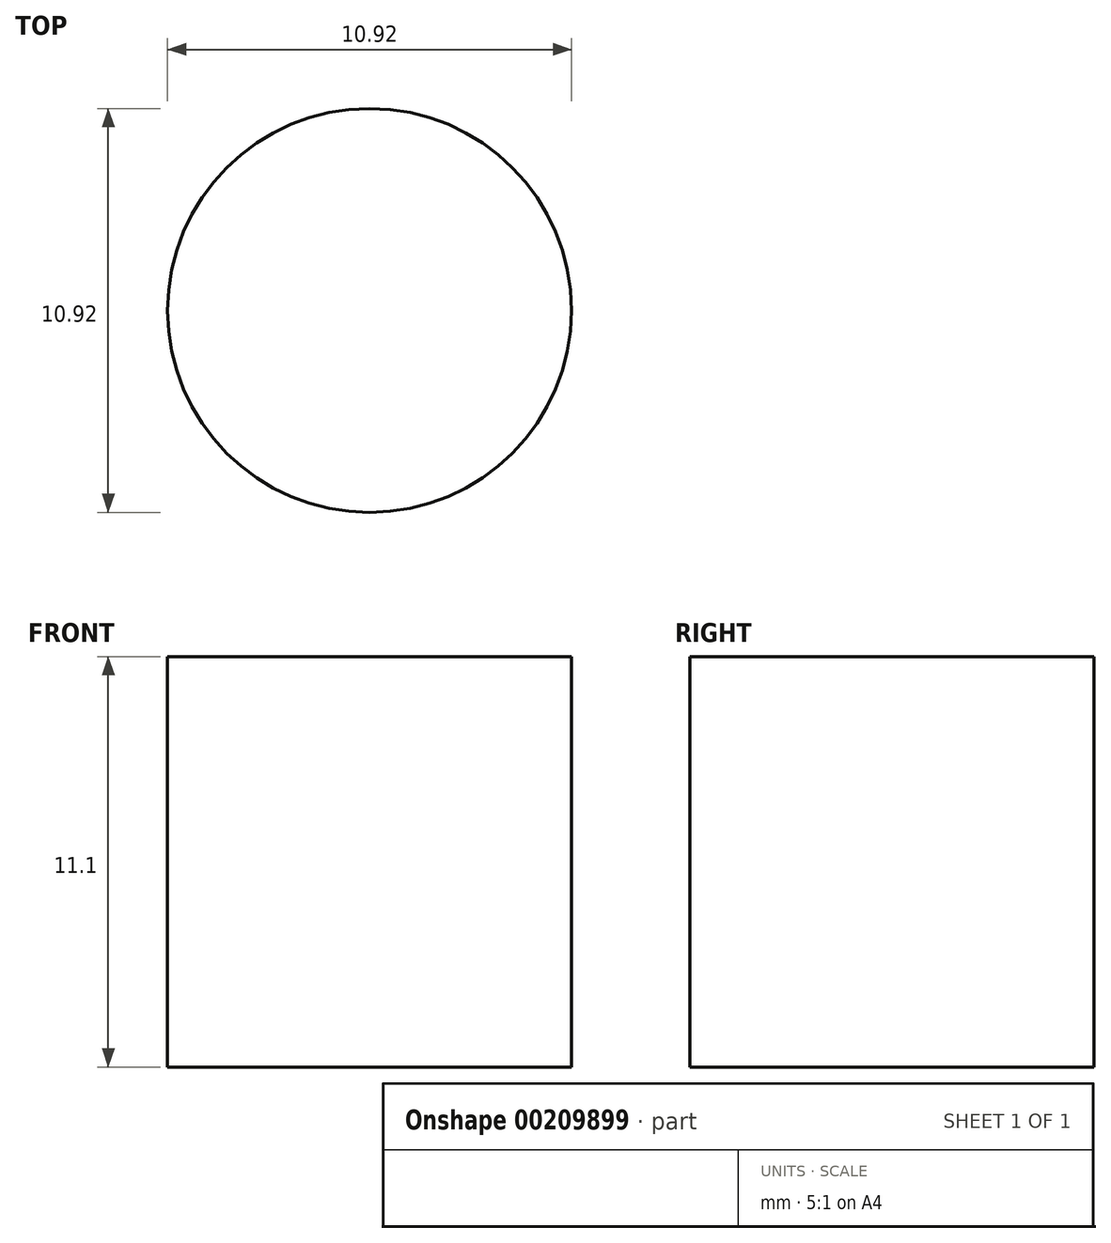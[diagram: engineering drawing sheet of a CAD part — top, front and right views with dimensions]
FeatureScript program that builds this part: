
annotation { "Feature Type Name" : "Feature", "Feature Type Description" : "" }
export const myFeature = defineFeature(function(context is Context, id is Id, definition is map)
    precondition{}
    {
        {
            var Q0;
            Q0=qCreatedBy(makeId("Top.planeOp"),FACE);
            var sketch = newSketch(context, id + "F0", { "sketchPlane" : qUnion([Q0])});
            skCircle(sketch, "E0", {"center": v(0, 0) * mm, "radius": 5.46 * mm});
            skSolve(sketch);
        }
        {
            var Q0;
            Q0=makeQuery(id+"F0.imprint","IMPRINT",FACE,{"disambiguationData":[TD([[makeQuery(id+"F0.imprint","IMPRINT",EDGE,{"derivedFrom":sQuery(id+"F0.wireOp",EDGE,"E0")}),1.0]])]});
            extrude(context, id + "F1", {"entities" : qUnion([Q0]), "depth" : 11.1 * mm});
        }
    });
